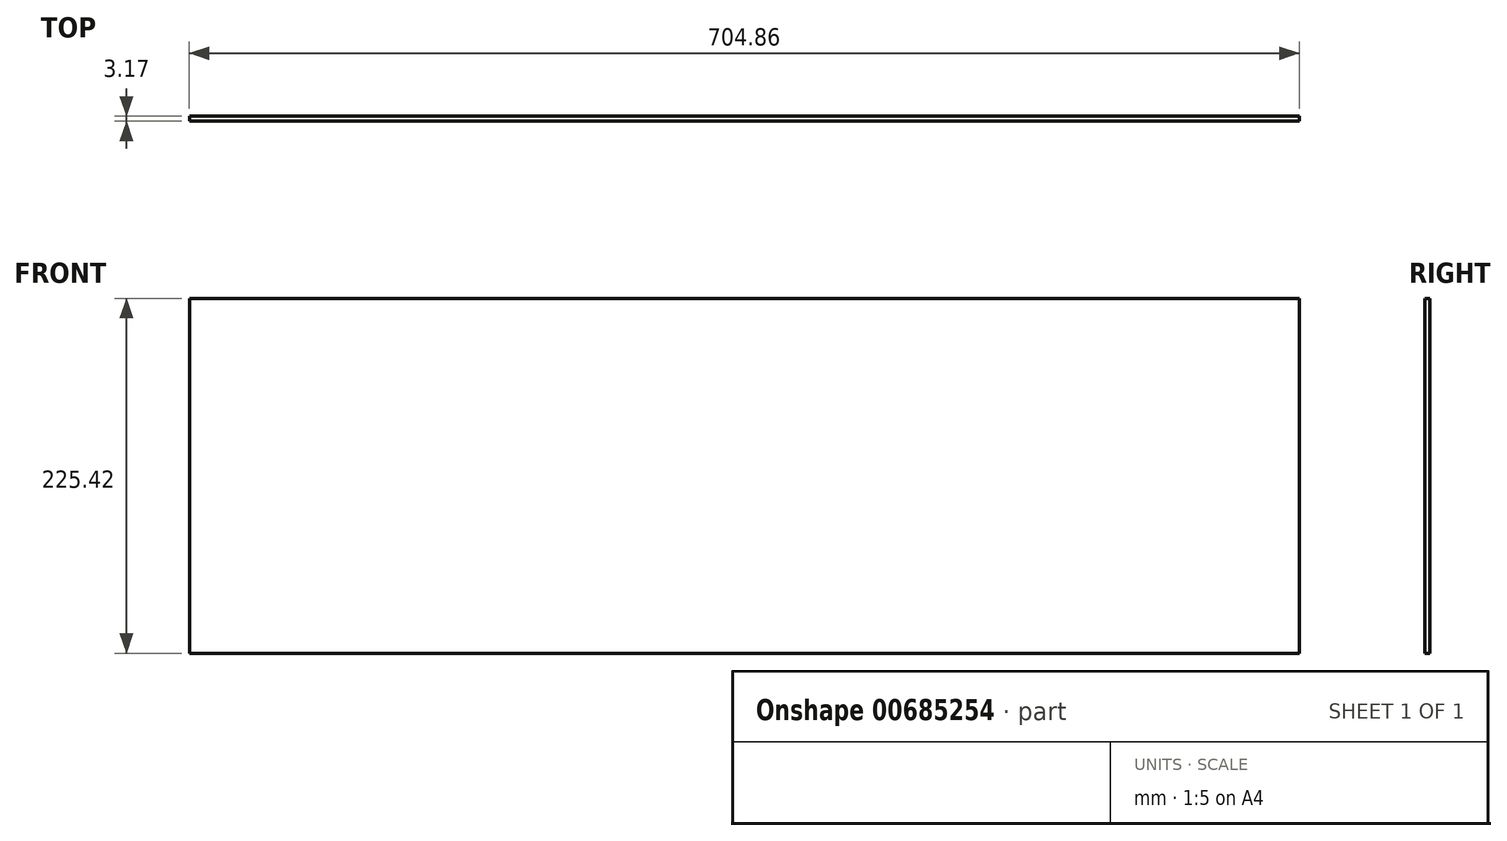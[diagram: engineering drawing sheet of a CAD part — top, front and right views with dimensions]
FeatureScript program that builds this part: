
annotation { "Feature Type Name" : "Feature", "Feature Type Description" : "" }
export const myFeature = defineFeature(function(context is Context, id is Id, definition is map)
    precondition{}
    {
        {
            var Q0;
            Q0=qCreatedBy(makeId("Front.planeOp"),FACE);
            var sketch = newSketch(context, id + "F0", { "sketchPlane" : qUnion([Q0])});
            skLineSegment(sketch, "E0.bottom", {"start": v(352.43, 112.71) * mm, "end": v(-352.43, 112.71) * mm});
            skLineSegment(sketch, "E0.top", {"start": v(352.43, -112.71) * mm, "end": v(-352.43, -112.71) * mm});
            skLineSegment(sketch, "E0.left", {"start": v(352.43, 112.71) * mm, "end": v(352.43, -112.71) * mm});
            skLineSegment(sketch, "E0.right", {"start": v(-352.43, 112.71) * mm, "end": v(-352.43, -112.71) * mm});
            skPoint(sketch, "E0.middle", {"position": v(0, 0) * mm});
            skSolve(sketch);
        }
        {
            var Q0;
            Q0=qSketchRegion(id+"F0",true);
            extrude(context, id + "F1", {"entities" : qUnion([Q0]), "depth" : 3.17 * mm, "offsetDistance" : 25.4 * mm});
        }
    });
